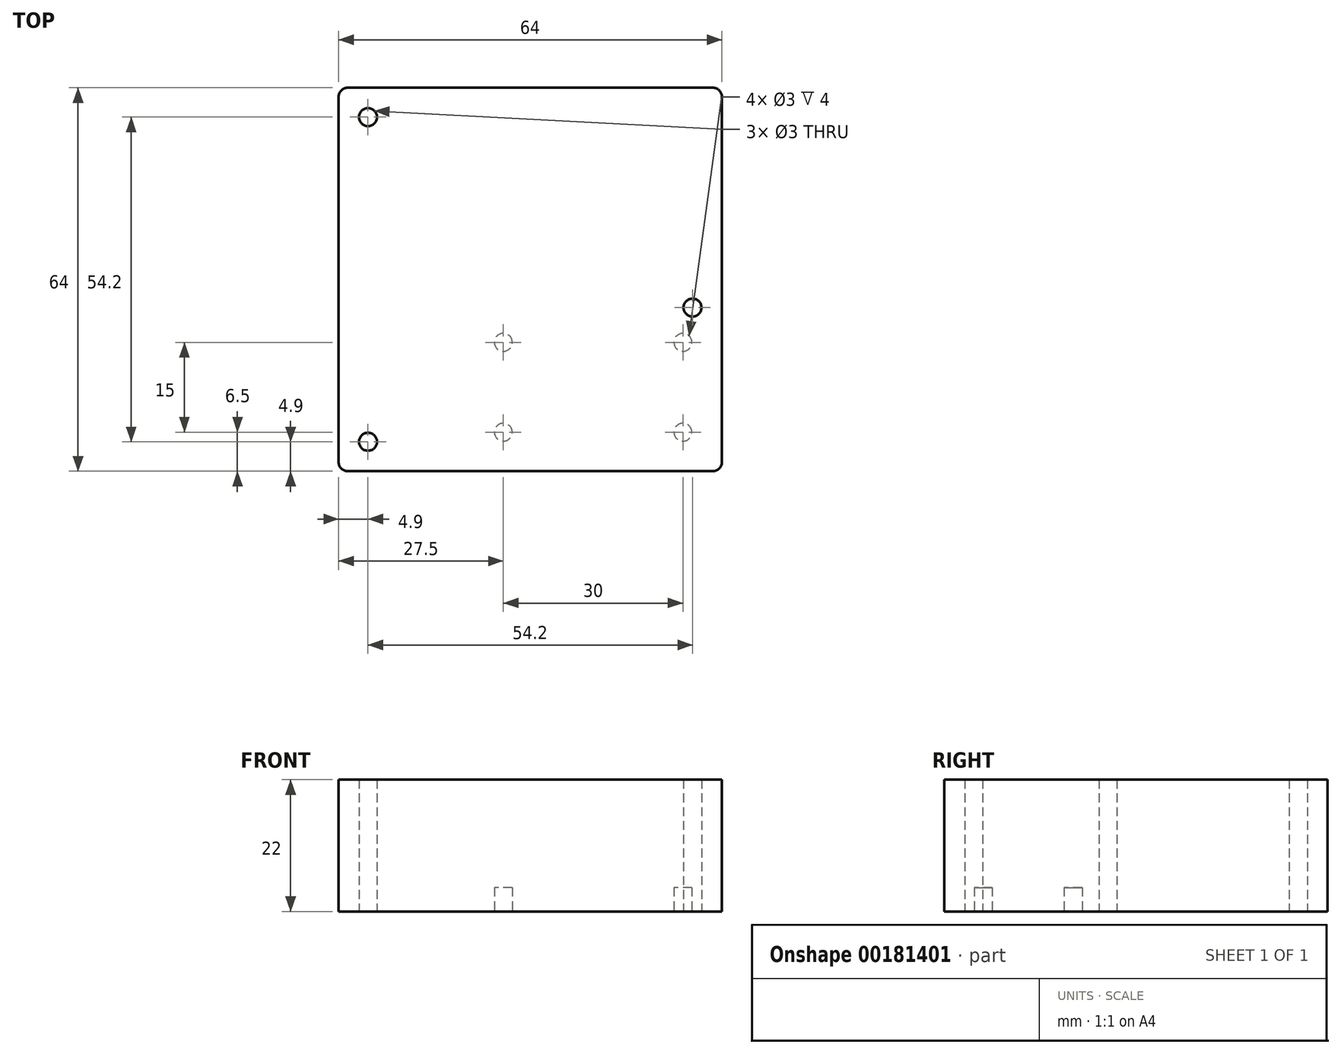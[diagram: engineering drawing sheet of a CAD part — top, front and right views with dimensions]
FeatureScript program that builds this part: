
annotation { "Feature Type Name" : "Feature", "Feature Type Description" : "" }
export const myFeature = defineFeature(function(context is Context, id is Id, definition is map)
    precondition{}
    {
        {
            var Q0;
            Q0=qCreatedBy(makeId("Top.planeOp"),FACE);
            var sketch = newSketch(context, id + "F0", { "sketchPlane" : qUnion([Q0])});
            skLineSegment(sketch, "E0.bottom", {"start": v(30.5, -32) * mm, "end": v(-30.5, -32) * mm});
            skLineSegment(sketch, "E0.top", {"start": v(30.5, 32) * mm, "end": v(-30.5, 32) * mm});
            skLineSegment(sketch, "E0.left", {"start": v(32, -30.5) * mm, "end": v(32, 30.5) * mm});
            skLineSegment(sketch, "E0.right", {"start": v(-32, -30.5) * mm, "end": v(-32, 30.5) * mm});
            skPoint(sketch, "E0.middle", {"position": v(0, 0) * mm});
            skPoint(sketch, "E1.visualSharp", {"position": v(-32, 32) * mm});
            skArc(sketch, "E1.filletArc", {"start": v(-30.5, 32) * mm, "mid": v(-31.56, 31.56) * mm, "end": v(-32, 30.5) * mm});
            skPoint(sketch, "E2.visualSharp", {"position": v(32, 32) * mm});
            skArc(sketch, "E2.filletArc", {"start": v(32, 30.5) * mm, "mid": v(31.56, 31.56) * mm, "end": v(30.5, 32) * mm});
            skPoint(sketch, "E3.visualSharp", {"position": v(32, -32) * mm});
            skArc(sketch, "E3.filletArc", {"start": v(30.5, -32) * mm, "mid": v(31.56, -31.56) * mm, "end": v(32, -30.5) * mm});
            skPoint(sketch, "E4.visualSharp", {"position": v(-32, -32) * mm});
            skArc(sketch, "E4.filletArc", {"start": v(-32, -30.5) * mm, "mid": v(-31.56, -31.56) * mm, "end": v(-30.5, -32) * mm});
            skLineSegment(sketch, "E5.bottom", {"start": v(-27.1, 27.1) * mm, "end": v(27.1, 27.1) * mm, "construction": true});
            skLineSegment(sketch, "E5.top", {"start": v(-27.1, -27.1) * mm, "end": v(27.1, -27.1) * mm, "construction": true});
            skLineSegment(sketch, "E5.left", {"start": v(-27.1, 27.1) * mm, "end": v(-27.1, -27.1) * mm, "construction": true});
            skLineSegment(sketch, "E5.right", {"start": v(27.1, 27.1) * mm, "end": v(27.1, -27.1) * mm, "construction": true});
            skCircle(sketch, "E6", {"center": v(27.1, -4.7) * mm, "radius": 1.5 * mm});
            skCircle(sketch, "E7", {"center": v(-27.1, -27.1) * mm, "radius": 1.5 * mm});
            skCircle(sketch, "E8", {"center": v(-27.1, 27.1) * mm, "radius": 1.5 * mm});
            skLineSegment(sketch, "E9.bottom", {"start": v(-4.5, -10.5) * mm, "end": v(25.5, -10.5) * mm, "construction": true});
            skLineSegment(sketch, "E9.top", {"start": v(-4.5, -25.5) * mm, "end": v(25.5, -25.5) * mm, "construction": true});
            skLineSegment(sketch, "E9.left", {"start": v(-4.5, -10.5) * mm, "end": v(-4.5, -25.5) * mm, "construction": true});
            skLineSegment(sketch, "E9.right", {"start": v(25.5, -10.5) * mm, "end": v(25.5, -25.5) * mm, "construction": true});
            skPoint(sketch, "E9.middle", {"position": v(10.5, -18) * mm});
            skCircle(sketch, "E10", {"center": v(25.5, -25.5) * mm, "radius": 1.5 * mm});
            skCircle(sketch, "E11", {"center": v(-4.5, -25.5) * mm, "radius": 1.5 * mm});
            skCircle(sketch, "E12", {"center": v(-4.5, -10.5) * mm, "radius": 1.5 * mm});
            skCircle(sketch, "E13", {"center": v(25.5, -10.5) * mm, "radius": 1.5 * mm});
            skSolve(sketch);
        }
        {
            var Q0;
            Q0=makeQuery(id+"F0.imprint","IMPRINT",FACE,{"disambiguationData":[TD([[makeQuery(id+"F0.imprint","IMPRINT",EDGE,{"derivedFrom":sQuery(id+"F0.wireOp",EDGE,"E0.bottom")}),-1.0]])]});
            var Q1;
            Q1=makeQuery(id+"F0.imprint","IMPRINT",FACE,{"disambiguationData":[TD([[makeQuery(id+"F0.imprint","IMPRINT",EDGE,{"derivedFrom":sQuery(id+"F0.wireOp",EDGE,"E10")}),1.0]])]});
            var Q2;
            Q2=makeQuery(id+"F0.imprint","IMPRINT",FACE,{"disambiguationData":[TD([[makeQuery(id+"F0.imprint","IMPRINT",EDGE,{"derivedFrom":sQuery(id+"F0.wireOp",EDGE,"E11")}),1.0]])]});
            var Q3;
            Q3=makeQuery(id+"F0.imprint","IMPRINT",FACE,{"disambiguationData":[TD([[makeQuery(id+"F0.imprint","IMPRINT",EDGE,{"derivedFrom":sQuery(id+"F0.wireOp",EDGE,"E12")}),1.0]])]});
            var Q4;
            Q4=makeQuery(id+"F0.imprint","IMPRINT",FACE,{"disambiguationData":[TD([[makeQuery(id+"F0.imprint","IMPRINT",EDGE,{"derivedFrom":sQuery(id+"F0.wireOp",EDGE,"E13")}),1.0]])]});
            extrude(context, id + "F1", {"entities" : qUnion([Q0, Q1, Q2, Q3, Q4]), "depth" : 22 * mm, "offsetDistance" : 25 * mm});
        }
        {
            var Q0;
            Q0=makeQuery(id+"F0.imprint","IMPRINT",FACE,{"disambiguationData":[TD([[makeQuery(id+"F0.imprint","IMPRINT",EDGE,{"derivedFrom":sQuery(id+"F0.wireOp",EDGE,"E13")}),1.0]])]});
            var Q1;
            Q1=makeQuery(id+"F0.imprint","IMPRINT",FACE,{"disambiguationData":[TD([[makeQuery(id+"F0.imprint","IMPRINT",EDGE,{"derivedFrom":sQuery(id+"F0.wireOp",EDGE,"E12")}),1.0]])]});
            var Q2;
            Q2=makeQuery(id+"F0.imprint","IMPRINT",FACE,{"disambiguationData":[TD([[makeQuery(id+"F0.imprint","IMPRINT",EDGE,{"derivedFrom":sQuery(id+"F0.wireOp",EDGE,"E11")}),1.0]])]});
            var Q3;
            Q3=makeQuery(id+"F0.imprint","IMPRINT",FACE,{"disambiguationData":[TD([[makeQuery(id+"F0.imprint","IMPRINT",EDGE,{"derivedFrom":sQuery(id+"F0.wireOp",EDGE,"E10")}),1.0]])]});
            extrude(context, id + "F2", {"entities" : qUnion([Q0, Q1, Q2, Q3]), "operationType" : NewBodyOperationType.REMOVE, "depth" : 4 * mm, "offsetDistance" : 25 * mm});
        }
    });
